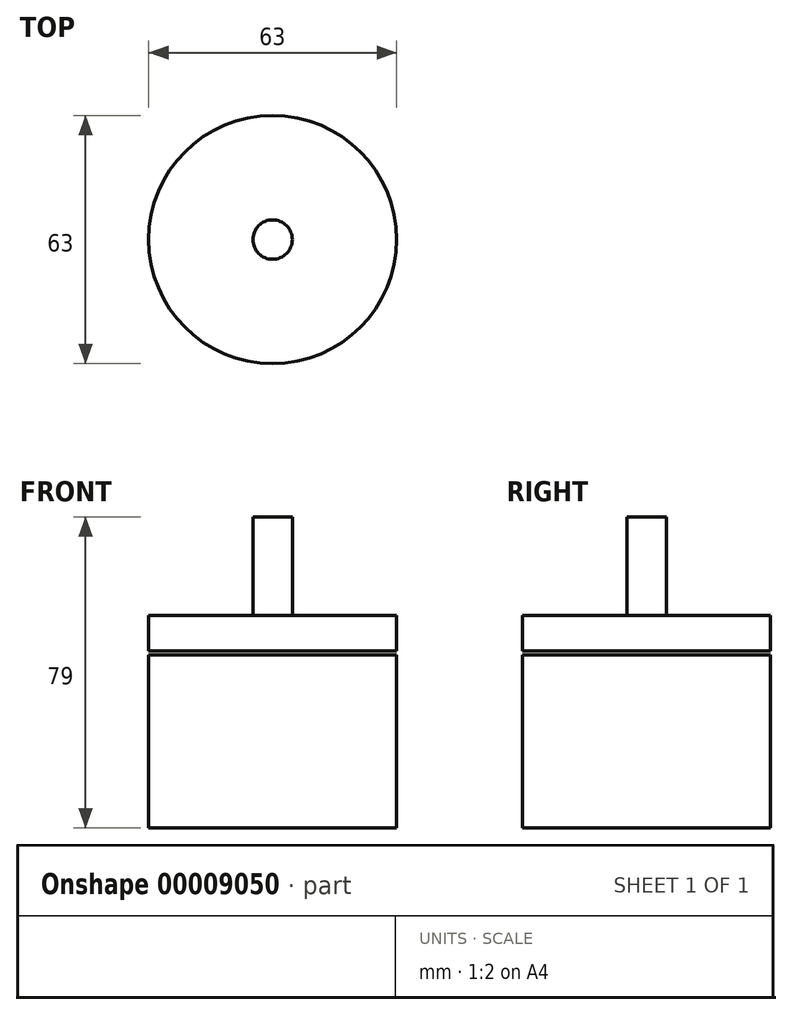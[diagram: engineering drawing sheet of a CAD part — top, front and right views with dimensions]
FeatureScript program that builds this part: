
annotation { "Feature Type Name" : "Feature", "Feature Type Description" : "" }
export const myFeature = defineFeature(function(context is Context, id is Id, definition is map)
    precondition{}
    {
        {
            var Q0;
            Q0=qCreatedBy(makeId("Top.planeOp"),FACE);
            var sketch = newSketch(context, id + "F0", { "sketchPlane" : qUnion([Q0])});
            skCircle(sketch, "E0", {"center": v(0, 0) * mm, "radius": 31.5 * mm});
            skSolve(sketch);
        }
        {
            var Q0;
            Q0 = qSketchRegion(id + "F0", true);
            extrude(context, id + "F1", {"entities" : qUnion([Q0]), "depth" : 44 * mm});
        }
        {
            var Q0;
            Q0=makeQuery(id+"F1.opExtrude","CAP_FACE",FACE,{"disambiguationData":[OSD([sQuery(id+"F0.wireOp",EDGE,"E0")])],"isStart":false});
            var sketch = newSketch(context, id + "F2", { "sketchPlane" : qUnion([Q0])});
            skCircle(sketch, "E1", {"center": v(0, 0) * mm, "radius": 31.5 * mm});
            skSolve(sketch);
        }
        {
            var Q0;
            Q0 = qSketchRegion(id + "F2", true);
            extrude(context, id + "F3", {"entities" : qUnion([Q0]), "operationType" : NewBodyOperationType.ADD, "depth" : 10 * mm, "hasSecondDirection" : true, "secondDirectionOppositeDirection" : false, "secondDirectionDepth" : 1 * mm});
        }
        {
            var Q0;
            Q0=makeQuery(id+"F3.opExtrude","CAP_FACE",FACE,{"disambiguationData":[OSD([sQuery(id+"F2.wireOp",EDGE,"E1")])],"isStart":false});
            var sketch = newSketch(context, id + "F4", { "sketchPlane" : qUnion([Q0])});
            skCircle(sketch, "E2", {"center": v(0, 0) * mm, "radius": 5 * mm});
            skSolve(sketch);
        }
        {
            var Q0;
            Q0 = qSketchRegion(id + "F4", true);
            extrude(context, id + "F5", {"entities" : qUnion([Q0]), "operationType" : NewBodyOperationType.ADD, "depth" : 25 * mm});
        }
    });
